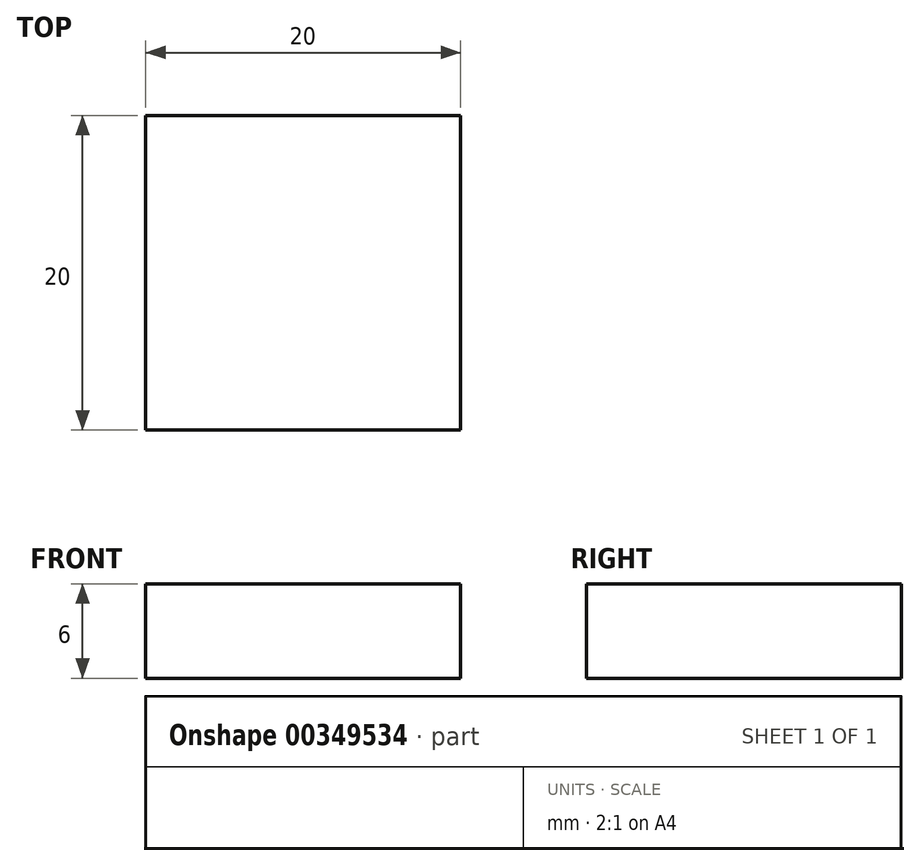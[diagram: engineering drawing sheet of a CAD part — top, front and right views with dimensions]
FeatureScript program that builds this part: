
annotation { "Feature Type Name" : "Feature", "Feature Type Description" : "" }
export const myFeature = defineFeature(function(context is Context, id is Id, definition is map)
    precondition{}
    {
        {
            var Q0;
            Q0=qCreatedBy(makeId("Top.planeOp"),FACE);
            var sketch = newSketch(context, id + "F0", { "sketchPlane" : qUnion([Q0])});
            skLineSegment(sketch, "E0.bottom", {"start": v(10, -10) * mm, "end": v(-10, -10) * mm});
            skLineSegment(sketch, "E0.top", {"start": v(10, 10) * mm, "end": v(-10, 10) * mm});
            skLineSegment(sketch, "E0.left", {"start": v(10, -10) * mm, "end": v(10, 10) * mm});
            skLineSegment(sketch, "E0.right", {"start": v(-10, -10) * mm, "end": v(-10, 10) * mm});
            skPoint(sketch, "E0.middle", {"position": v(0, 0) * mm});
            skSolve(sketch);
        }
        {
            var Q0;
            Q0=makeQuery(id+"F0.imprint","IMPRINT",FACE,{"disambiguationData":[TD([[makeQuery(id+"F0.imprint","IMPRINT",EDGE,{"derivedFrom":sQuery(id+"F0.wireOp",EDGE,"E0.bottom")}),-1.0]])]});
            extrude(context, id + "F1", {"entities" : qUnion([Q0]), "depth" : 6 * mm});
        }
    });
